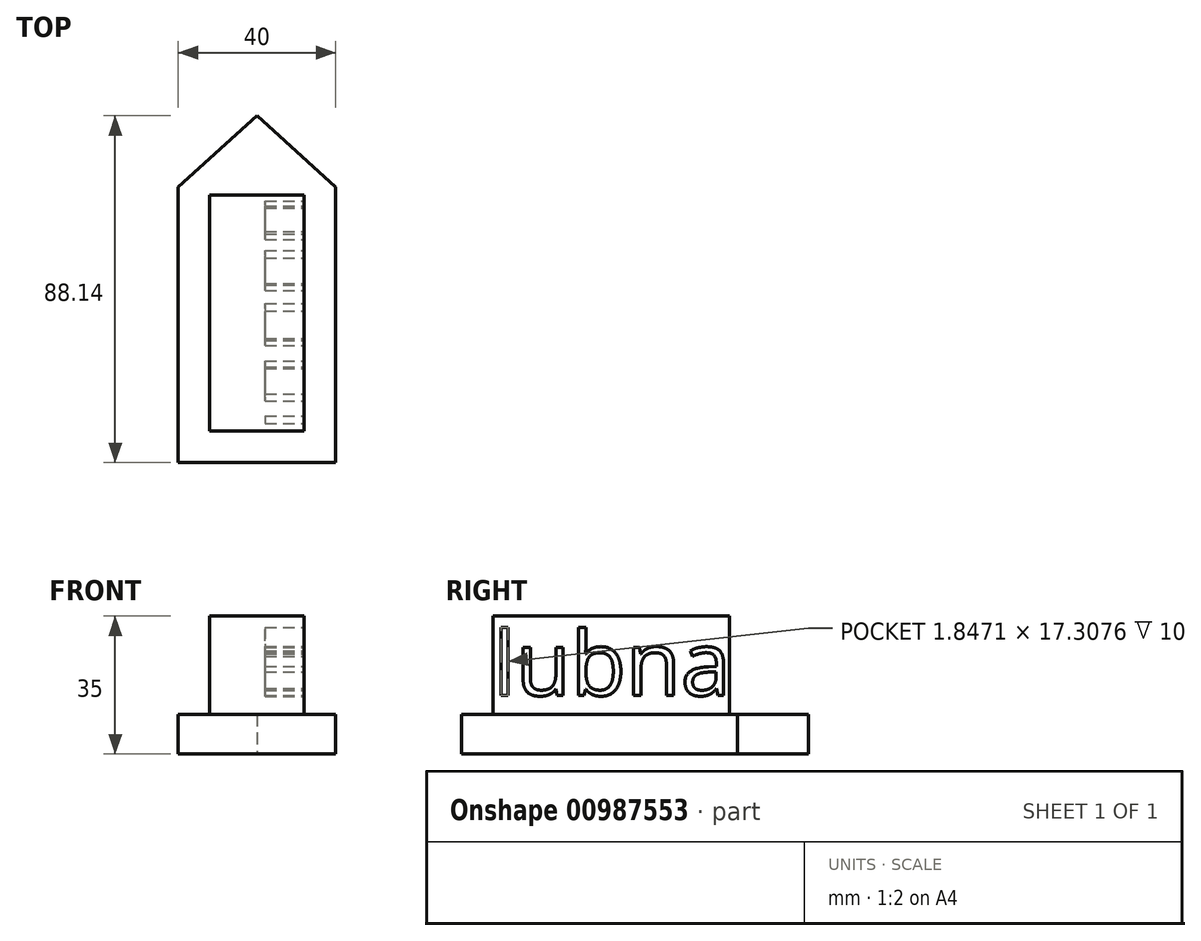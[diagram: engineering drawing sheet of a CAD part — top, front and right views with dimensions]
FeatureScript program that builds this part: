
annotation { "Feature Type Name" : "Feature", "Feature Type Description" : "" }
export const myFeature = defineFeature(function(context is Context, id is Id, definition is map)
    precondition{}
    {
        {
            var Q0;
            Q0=qCreatedBy(makeId("Top.planeOp"),FACE);
            var sketch = newSketch(context, id + "F0", { "sketchPlane" : qUnion([Q0])});
            skLineSegment(sketch, "E0", {"start": v(20, 45.53) * mm, "end": v(20, -24.47) * mm});
            skLineSegment(sketch, "E1", {"start": v(20, -24.47) * mm, "end": v(-20, -24.47) * mm});
            skLineSegment(sketch, "E2", {"start": v(-20, -24.47) * mm, "end": v(-20, 45.53) * mm});
            skLineSegment(sketch, "E3", {"start": v(-20, 45.53) * mm, "end": v(0, 63.67) * mm});
            skLineSegment(sketch, "E4", {"start": v(0, 63.67) * mm, "end": v(20, 45.53) * mm});
            skSolve(sketch);
        }
        {
            var Q0;
            Q0=makeQuery(id+"F0.imprint","IMPRINT",FACE,{"disambiguationData":[TD([[makeQuery(id+"F0.imprint","IMPRINT",EDGE,{"derivedFrom":sQuery(id+"F0.wireOp",EDGE,"E0")}),-1.0]])]});
            extrude(context, id + "F1", {"entities" : qUnion([Q0]), "depth" : 10 * mm, "offsetDistance" : 25 * mm});
        }
        {
            var Q0;
            Q0=makeQuery(id+"F1.opExtrude","CAP_FACE",FACE,{"disambiguationData":[OSD([sQuery(id+"F0.wireOp",EDGE,"E0"),sQuery(id+"F0.wireOp",EDGE,"E1"),sQuery(id+"F0.wireOp",EDGE,"E2"),sQuery(id+"F0.wireOp",EDGE,"E3"),sQuery(id+"F0.wireOp",EDGE,"E4")])],"isStart":false});
            var sketch = newSketch(context, id + "F2", { "sketchPlane" : qUnion([Q0])});
            skLineSegment(sketch, "E5", {"start": v(-12, 43.53) * mm, "end": v(-12, -16.47) * mm});
            skLineSegment(sketch, "E6", {"start": v(-12, -16.47) * mm, "end": v(12, -16.47) * mm});
            skLineSegment(sketch, "E7", {"start": v(12, -16.47) * mm, "end": v(12, 43.53) * mm});
            skLineSegment(sketch, "E8", {"start": v(12, 43.53) * mm, "end": v(-12, 43.53) * mm});
            skSolve(sketch);
        }
        {
            var Q0;
            Q0=makeQuery(id+"F2.imprint","IMPRINT",FACE,{"disambiguationData":[TD([[makeQuery(id+"F2.imprint","IMPRINT",EDGE,{"derivedFrom":sQuery(id+"F2.wireOp",EDGE,"E5")}),1.0]])]});
            extrude(context, id + "F3", {"entities" : qUnion([Q0]), "operationType" : NewBodyOperationType.ADD, "depth" : 25 * mm, "offsetDistance" : 25 * mm});
        }
        {
            var Q0;
            Q0=makeQuery(id+"F3.opExtrude","CAP_FACE",FACE,{"disambiguationData":[OSD([sQuery(id+"F2.wireOp",EDGE,"E5"),sQuery(id+"F2.wireOp",EDGE,"E6"),sQuery(id+"F2.wireOp",EDGE,"E7"),sQuery(id+"F2.wireOp",EDGE,"E8")])],"isStart":false});
            var sketch = newSketch(context, id + "F4", { "sketchPlane" : qUnion([Q0])});
            skCircle(sketch, "E9", {"center": v(0, 0) * mm, "radius": 4.5 * mm});
            skCircle(sketch, "E10", {"center": v(0, 16.5) * mm, "radius": 4.5 * mm});
            skCircle(sketch, "E11", {"center": v(0, 32.72) * mm, "radius": 4.5 * mm});
            skSolve(sketch);
        }
        {
            var Q0;
            Q0=sQuery(id+"F4.wireOp",EDGE,"E11");
            var Q1;
            Q1=sQuery(id+"F4.wireOp",EDGE,"E10");
            var Q2;
            Q2=sQuery(id+"F4.wireOp",EDGE,"E9");
            extrude(context, id + "F5", {"bodyType" : ToolBodyType.SURFACE, "surfaceEntities" : qUnion([Q0, Q1, Q2]), "depth" : 15 * mm, "offsetDistance" : 25 * mm});
        }
        {
            var Q0;
            Q0=makeQuery(id+"F3.opExtrude","SWEPT_FACE",FACE,{"disambiguationData":[OSD([sQuery(id+"F2.wireOp",EDGE,"E7")])]});
            var sketch = newSketch(context, id + "F6", { "sketchPlane" : qUnion([Q0])});
            skText(sketch, "E12", { "text": "lubna", "fontName": "OpenSans-Regular.ttf"});
            const initialGuessF6  = {"E12": [-0.01647, 0.01484, 1, 0, 0.0164]};
            skSetInitialGuess(sketch, initialGuessF6);
            skSolve(sketch);
        }
        {
            var Q0;
            Q0 = qSketchRegion(id + "F6", true);
            extrude(context, id + "F7", {"entities" : qUnion([Q0]), "operationType" : NewBodyOperationType.REMOVE, "oppositeDirection" : true, "depth" : 10 * mm, "offsetDistance" : 25 * mm});
        }
    });
